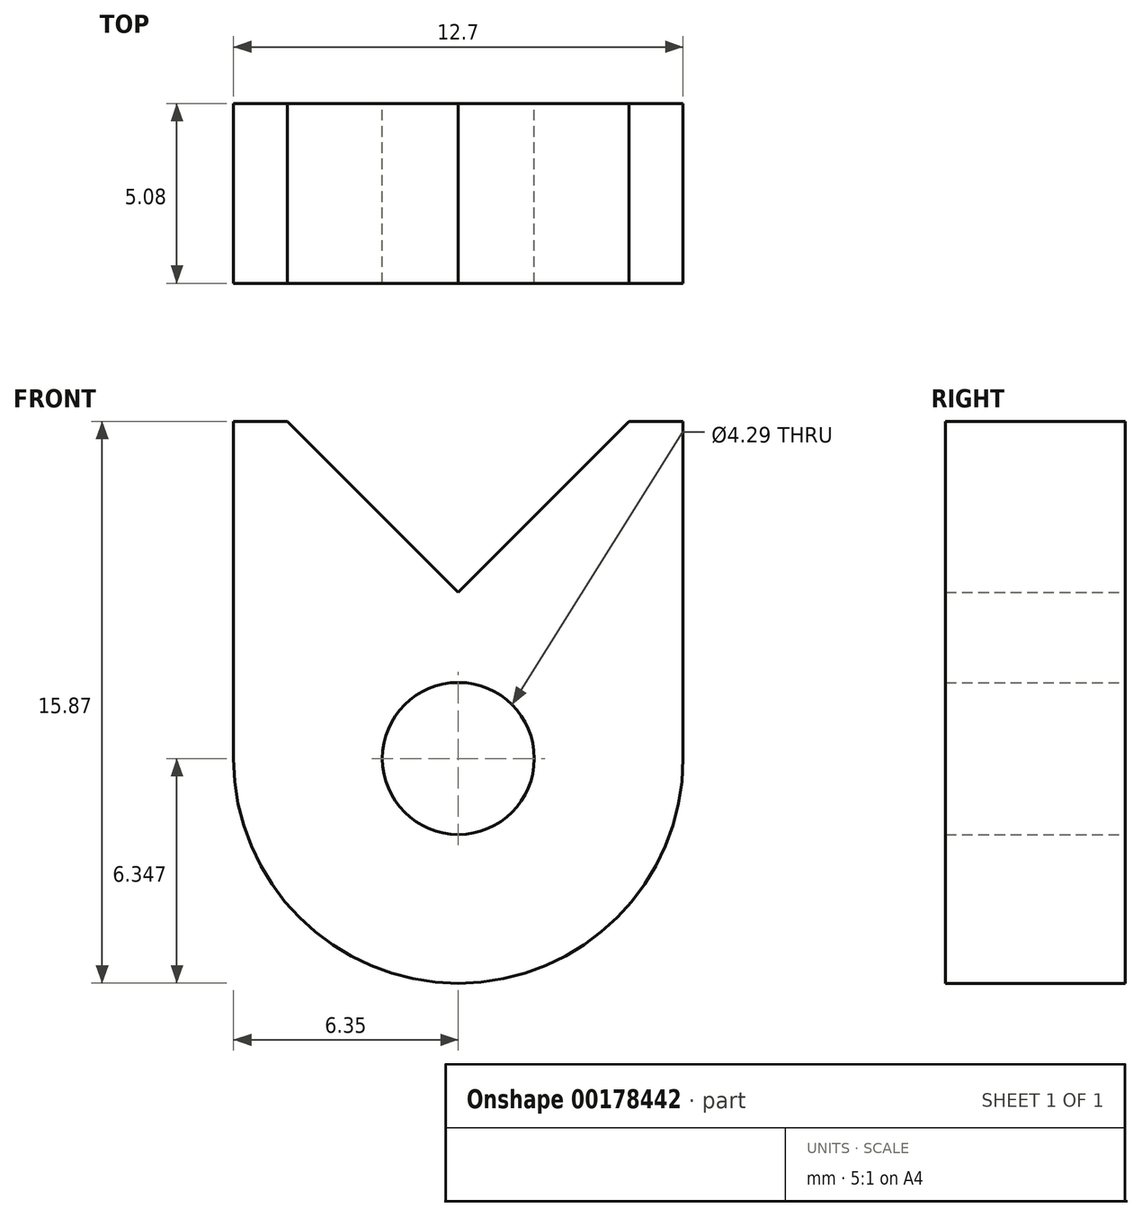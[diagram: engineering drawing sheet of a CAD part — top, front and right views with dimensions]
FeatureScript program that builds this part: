
annotation { "Feature Type Name" : "Feature", "Feature Type Description" : "" }
export const myFeature = defineFeature(function(context is Context, id is Id, definition is map)
    precondition{}
    {
        {
            var Q0;
            Q0=qCreatedBy(makeId("Front.planeOp"),FACE);
            var sketch = newSketch(context, id + "F0", { "sketchPlane" : qUnion([Q0])});
            skLineSegment(sketch, "E0.bottom", {"start": v(6.35, 4.76) * mm, "end": v(-6.35, 4.76) * mm, "construction": true});
            skLineSegment(sketch, "E0.top", {"start": v(6.35, -4.76) * mm, "end": v(-6.35, -4.76) * mm, "construction": true});
            skLineSegment(sketch, "E0.left", {"start": v(6.35, 4.76) * mm, "end": v(6.35, -4.76) * mm});
            skLineSegment(sketch, "E0.right", {"start": v(-6.35, 4.76) * mm, "end": v(-6.35, -4.76) * mm});
            skPoint(sketch, "E0.middle", {"position": v(0, 0) * mm});
            skArc(sketch, "E1", {"start": v(-6.35, -4.76) * mm, "mid": v(0, -11.11) * mm, "end": v(6.35, -4.76) * mm});
            skLineSegment(sketch, "E2", {"start": v(-6.35, 4.76) * mm, "end": v(-4.83, 4.76) * mm});
            skLineSegment(sketch, "E3", {"start": v(-4.83, 4.76) * mm, "end": v(0, -0.06) * mm});
            skLineSegment(sketch, "E4", {"start": v(0, -0.06) * mm, "end": v(4.83, 4.76) * mm});
            skLineSegment(sketch, "E5", {"start": v(4.83, 4.76) * mm, "end": v(6.35, 4.76) * mm});
            skCircle(sketch, "E6", {"center": v(0, -4.76) * mm, "radius": 2.15 * mm});
            skSolve(sketch);
        }
        {
            var Q0;
            Q0 = qSketchRegion(id + "F0", true);
            extrude(context, id + "F1", {"entities" : qUnion([Q0]), "depth" : 5.08 * mm});
        }
    });
